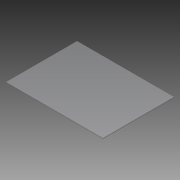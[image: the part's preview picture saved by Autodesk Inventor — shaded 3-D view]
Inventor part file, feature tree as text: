
AUTODESK INVENTOR PART (.ipt)
format: ipt  version: 2014 SP1 (Build 180222100, 222)  size: 69,120 bytes
history: native  units: in
note: dims shown in document units (in); Inventor stores cm internally (conversion verified against a paired STEP export)
features: extrude x1, sketch x1
ambient origin geometry x8: Origin, YZ Plane, XZ Plane, XY Plane, X Axis, Y Axis, Z Axis, Center Point
bodies: Solid1 (feature_tree)
feature tree (2):
  extrude  "Extrusion1"  Depth=5.5in
  sketch  "Sketch1"  dims[d0=7.5in d1=5.5in d2=0.0625in d3=0.0in]
